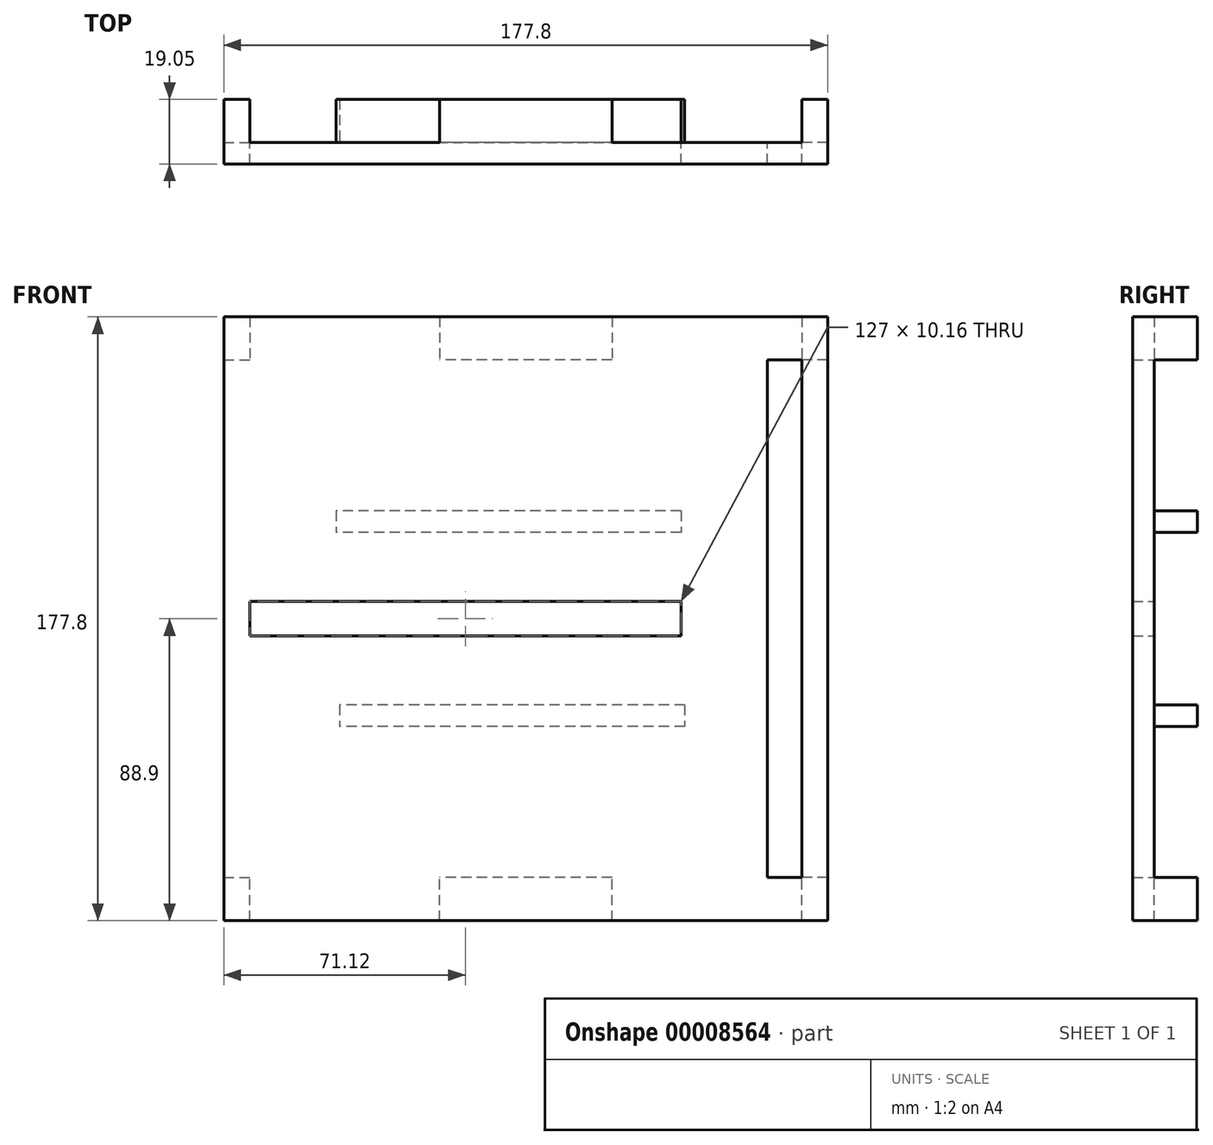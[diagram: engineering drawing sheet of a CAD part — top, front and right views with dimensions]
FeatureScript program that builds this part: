
annotation { "Feature Type Name" : "Feature", "Feature Type Description" : "" }
export const myFeature = defineFeature(function(context is Context, id is Id, definition is map)
    precondition{}
    {
        {
            var Q0;
            Q0=qCreatedBy(makeId("Front.planeOp"),FACE);
            var sketch = newSketch(context, id + "F0", { "sketchPlane" : qUnion([Q0])});
            skLineSegment(sketch, "E0.bottom", {"start": v(-88.9, 88.9) * mm, "end": v(88.9, 88.9) * mm});
            skLineSegment(sketch, "E0.top", {"start": v(-88.9, -88.9) * mm, "end": v(88.9, -88.9) * mm});
            skLineSegment(sketch, "E0.left", {"start": v(-88.9, 88.9) * mm, "end": v(-88.9, -88.9) * mm});
            skLineSegment(sketch, "E0.right", {"start": v(88.9, 88.9) * mm, "end": v(88.9, -88.9) * mm});
            skLineSegment(sketch, "E1.bottom", {"start": v(-81.28, 5.08) * mm, "end": v(45.72, 5.08) * mm});
            skLineSegment(sketch, "E1.top", {"start": v(-81.28, -5.08) * mm, "end": v(45.72, -5.08) * mm});
            skLineSegment(sketch, "E1.left", {"start": v(-81.28, 5.08) * mm, "end": v(-81.28, -5.08) * mm});
            skLineSegment(sketch, "E1.right", {"start": v(45.72, 5.08) * mm, "end": v(45.72, -5.08) * mm});
            skLineSegment(sketch, "E2.bottom", {"start": v(71.12, 76.2) * mm, "end": v(81.28, 76.2) * mm});
            skLineSegment(sketch, "E2.top", {"start": v(71.12, -76.2) * mm, "end": v(81.28, -76.2) * mm});
            skLineSegment(sketch, "E2.left", {"start": v(71.12, 76.2) * mm, "end": v(71.12, -76.2) * mm});
            skLineSegment(sketch, "E2.right", {"start": v(81.28, 76.2) * mm, "end": v(81.28, -76.2) * mm});
            skSolve(sketch);
        }
        {
            var Q0;
            Q0 = qSketchRegion(id + "F0", true);
            extrude(context, id + "F1", {"entities" : qUnion([Q0]), "depth" : 6.35 * mm});
        }
        {
            var Q0;
            Q0=makeQuery(id+"F1.opExtrude","CAP_FACE",FACE,{"disambiguationData":[OSD([sQuery(id+"F0.wireOp",EDGE,"E0.bottom"),sQuery(id+"F0.wireOp",EDGE,"E0.top"),sQuery(id+"F0.wireOp",EDGE,"E0.left"),sQuery(id+"F0.wireOp",EDGE,"E0.right"),sQuery(id+"F0.wireOp",EDGE,"E1.bottom"),sQuery(id+"F0.wireOp",EDGE,"E1.top"),sQuery(id+"F0.wireOp",EDGE,"E1.left"),sQuery(id+"F0.wireOp",EDGE,"E1.right"),sQuery(id+"F0.wireOp",EDGE,"E2.bottom"),sQuery(id+"F0.wireOp",EDGE,"E2.top"),sQuery(id+"F0.wireOp",EDGE,"E2.left"),sQuery(id+"F0.wireOp",EDGE,"E2.right")])],"isStart":true});
            var sketch = newSketch(context, id + "F2", { "sketchPlane" : qUnion([Q0])});
            skLineSegment(sketch, "E3.bottom", {"start": v(-88.9, 88.9) * mm, "end": v(-81.28, 88.9) * mm});
            skLineSegment(sketch, "E3.top", {"start": v(-88.9, 76.2) * mm, "end": v(-81.28, 76.2) * mm});
            skLineSegment(sketch, "E3.left", {"start": v(-88.9, 88.9) * mm, "end": v(-88.9, 76.2) * mm});
            skLineSegment(sketch, "E3.right", {"start": v(-81.28, 88.9) * mm, "end": v(-81.28, 76.2) * mm});
            skLineSegment(sketch, "E4.bottom", {"start": v(-88.9, -88.9) * mm, "end": v(-81.28, -88.9) * mm});
            skLineSegment(sketch, "E4.top", {"start": v(-88.9, -76.2) * mm, "end": v(-81.28, -76.2) * mm});
            skLineSegment(sketch, "E4.left", {"start": v(-88.9, -88.9) * mm, "end": v(-88.9, -76.2) * mm});
            skLineSegment(sketch, "E4.right", {"start": v(-81.28, -88.9) * mm, "end": v(-81.28, -76.2) * mm});
            skLineSegment(sketch, "E5.bottom", {"start": v(88.9, 88.9) * mm, "end": v(81.28, 88.9) * mm});
            skLineSegment(sketch, "E5.top", {"start": v(88.9, 76.2) * mm, "end": v(81.28, 76.2) * mm});
            skLineSegment(sketch, "E5.left", {"start": v(88.9, 88.9) * mm, "end": v(88.9, 76.2) * mm});
            skLineSegment(sketch, "E5.right", {"start": v(81.28, 88.9) * mm, "end": v(81.28, 76.2) * mm});
            skLineSegment(sketch, "E6.bottom", {"start": v(88.9, -88.9) * mm, "end": v(81.28, -88.9) * mm});
            skLineSegment(sketch, "E6.top", {"start": v(88.9, -76.2) * mm, "end": v(81.28, -76.2) * mm});
            skLineSegment(sketch, "E6.left", {"start": v(88.9, -88.9) * mm, "end": v(88.9, -76.2) * mm});
            skLineSegment(sketch, "E6.right", {"start": v(81.28, -88.9) * mm, "end": v(81.28, -76.2) * mm});
            skLineSegment(sketch, "E7.bottom", {"start": v(-25.4, 88.9) * mm, "end": v(25.4, 88.9) * mm});
            skLineSegment(sketch, "E7.top", {"start": v(-25.4, 76.2) * mm, "end": v(25.4, 76.2) * mm});
            skLineSegment(sketch, "E7.left", {"start": v(-25.4, 88.9) * mm, "end": v(-25.4, 76.2) * mm});
            skLineSegment(sketch, "E7.right", {"start": v(25.4, 88.9) * mm, "end": v(25.4, 76.2) * mm});
            skLineSegment(sketch, "E8.bottom", {"start": v(-25.4, -88.9) * mm, "end": v(25.4, -88.9) * mm});
            skLineSegment(sketch, "E8.top", {"start": v(-25.4, -76.2) * mm, "end": v(25.4, -76.2) * mm});
            skLineSegment(sketch, "E8.left", {"start": v(-25.4, -88.9) * mm, "end": v(-25.4, -76.2) * mm});
            skLineSegment(sketch, "E8.right", {"start": v(25.4, -88.9) * mm, "end": v(25.4, -76.2) * mm});
            skPoint(sketch, "E9", {"position": v(0, 76.2) * mm});
            skPoint(sketch, "E10", {"position": v(0, -76.2) * mm});
            skSolve(sketch);
        }
        {
            var Q0;
            Q0 = qSketchRegion(id + "F2", true);
            extrude(context, id + "F3", {"entities" : qUnion([Q0]), "operationType" : NewBodyOperationType.ADD, "depth" : 12.7 * mm});
        }
        {
            var Q0;
            {var subQ0=sQuery(id+"F0.wireOp",EDGE,"E0.bottom");var subQ1=sQuery(id+"F0.wireOp",EDGE,"E0.top");var subQ2=sQuery(id+"F0.wireOp",EDGE,"E0.left");var subQ3=sQuery(id+"F0.wireOp",EDGE,"E1.bottom");var subQ4=sQuery(id+"F0.wireOp",EDGE,"E1.top");var subQ5=sQuery(id+"F0.wireOp",EDGE,"E1.left");var subQ6=sQuery(id+"F0.wireOp",EDGE,"E1.right");var subQ7=sQuery(id+"F0.wireOp",EDGE,"E2.bottom");var subQ8=sQuery(id+"F0.wireOp",EDGE,"E2.top");var subQ9=sQuery(id+"F0.wireOp",EDGE,"E2.left");var subQ10=sQuery(id+"F0.wireOp",EDGE,"E2.right");var subQ11=makeQuery(id+"F1.opExtrude","CAP_FACE",FACE,{"disambiguationData":[OSD([subQ0,subQ1,subQ2,sQuery(id+"F0.wireOp",EDGE,"E0.right"),subQ3,subQ4,subQ5,subQ6,subQ7,subQ8,subQ9,subQ10])],"isStart":true});Q0=makeQuery(id+"F3.boolean.opBoolean","SPLIT",FACE,{"disambiguationData":[TD([makeQuery(id+"F1.opExtrude","SWEPT_FACE",FACE,{"disambiguationData":[OSD([subQ0])]})])],"derivedFrom":subQ11});}
            var sketch = newSketch(context, id + "F4", { "sketchPlane" : qUnion([Q0])});
            skLineSegment(sketch, "E11.bottom", {"start": v(-45.72, 31.75) * mm, "end": v(55.88, 31.75) * mm});
            skLineSegment(sketch, "E11.top", {"start": v(-45.72, 25.4) * mm, "end": v(55.88, 25.4) * mm});
            skLineSegment(sketch, "E11.left", {"start": v(-45.72, 31.75) * mm, "end": v(-45.72, 25.4) * mm});
            skLineSegment(sketch, "E11.right", {"start": v(55.88, 31.75) * mm, "end": v(55.88, 25.4) * mm});
            skLineSegment(sketch, "E12.bottom", {"start": v(-46.8, -25.4) * mm, "end": v(54.8, -25.4) * mm});
            skLineSegment(sketch, "E12.top", {"start": v(-46.8, -31.75) * mm, "end": v(54.8, -31.75) * mm});
            skLineSegment(sketch, "E12.left", {"start": v(-46.8, -25.4) * mm, "end": v(-46.8, -31.75) * mm});
            skLineSegment(sketch, "E12.right", {"start": v(54.8, -25.4) * mm, "end": v(54.8, -31.75) * mm});
            skSolve(sketch);
        }
        {
            var Q0;
            Q0 = qSketchRegion(id + "F4", true);
            extrude(context, id + "F5", {"entities" : qUnion([Q0]), "operationType" : NewBodyOperationType.ADD, "depth" : 12.7 * mm});
        }
    });
